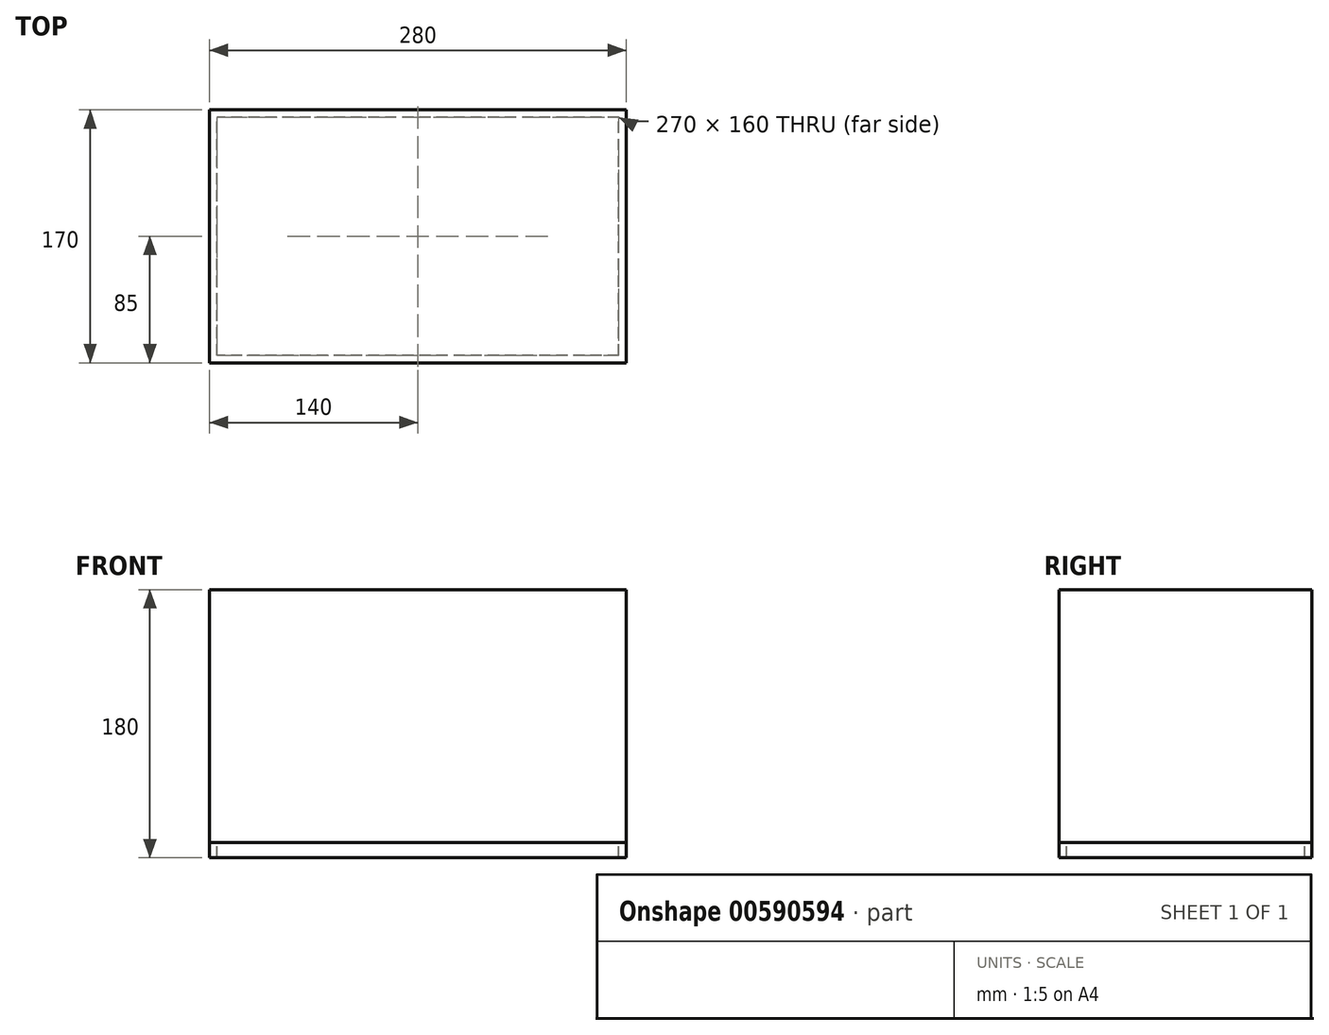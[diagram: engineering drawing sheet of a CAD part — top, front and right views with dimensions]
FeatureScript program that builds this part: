
annotation { "Feature Type Name" : "Feature", "Feature Type Description" : "" }
export const myFeature = defineFeature(function(context is Context, id is Id, definition is map)
    precondition{}
    {
        {
            var Q0;
            Q0=qCreatedBy(makeId("Top.planeOp"),FACE);
            var sketch = newSketch(context, id + "F0", { "sketchPlane" : qUnion([Q0])});
            skLineSegment(sketch, "E0.bottom", {"start": v(140, 85) * mm, "end": v(-140, 85) * mm});
            skLineSegment(sketch, "E0.top", {"start": v(140, -85) * mm, "end": v(-140, -85) * mm});
            skLineSegment(sketch, "E0.left", {"start": v(140, 85) * mm, "end": v(140, -85) * mm});
            skLineSegment(sketch, "E0.right", {"start": v(-140, 85) * mm, "end": v(-140, -85) * mm});
            skPoint(sketch, "E0.middle", {"position": v(0, 0) * mm});
            skSolve(sketch);
        }
        {
            var Q0;
            Q0=makeQuery(id+"F0.imprint","IMPRINT",FACE,{"disambiguationData":[TD([[makeQuery(id+"F0.imprint","IMPRINT",EDGE,{"derivedFrom":sQuery(id+"F0.wireOp",EDGE,"E0.bottom")}),1.0]])]});
            extrude(context, id + "F1", {"entities" : qUnion([Q0]), "depth" : 170 * mm, "offsetDistance" : 25 * mm});
        }
        {
            var Q0;
            Q0=makeQuery(id+"F1.opExtrude","CAP_FACE",FACE,{"disambiguationData":[OSD([sQuery(id+"F0.wireOp",EDGE,"E0.bottom"),sQuery(id+"F0.wireOp",EDGE,"E0.top"),sQuery(id+"F0.wireOp",EDGE,"E0.left"),sQuery(id+"F0.wireOp",EDGE,"E0.right")])],"isStart":true});
            var sketch = newSketch(context, id + "F2", { "sketchPlane" : qUnion([Q0])});
            skLineSegment(sketch, "E1.bottom", {"start": v(-140, 85) * mm, "end": v(140, 85) * mm});
            skLineSegment(sketch, "E1.top", {"start": v(-140, -85) * mm, "end": v(140, -85) * mm});
            skLineSegment(sketch, "E1.left", {"start": v(-140, 85) * mm, "end": v(-140, -85) * mm});
            skLineSegment(sketch, "E1.right", {"start": v(140, 85) * mm, "end": v(140, -85) * mm});
            skPoint(sketch, "E1.middle", {"position": v(0, 0) * mm});
            skLineSegment(sketch, "E2.bottom", {"start": v(135, 80) * mm, "end": v(-135, 80) * mm});
            skLineSegment(sketch, "E2.top", {"start": v(135, -80) * mm, "end": v(-135, -80) * mm});
            skLineSegment(sketch, "E2.left", {"start": v(135, 80) * mm, "end": v(135, -80) * mm});
            skLineSegment(sketch, "E2.right", {"start": v(-135, 80) * mm, "end": v(-135, -80) * mm});
            skSolve(sketch);
        }
        {
            var Q0;
            Q0=makeQuery(id+"F2.imprint","IMPRINT",FACE,{"disambiguationData":[TD([[makeQuery(id+"F2.imprint","IMPRINT",EDGE,{"derivedFrom":sQuery(id+"F2.wireOp",EDGE,"E1.bottom")}),1.0]])]});
            extrude(context, id + "F3", {"entities" : qUnion([Q0]), "depth" : 10 * mm, "offsetDistance" : 25 * mm});
        }
    });
